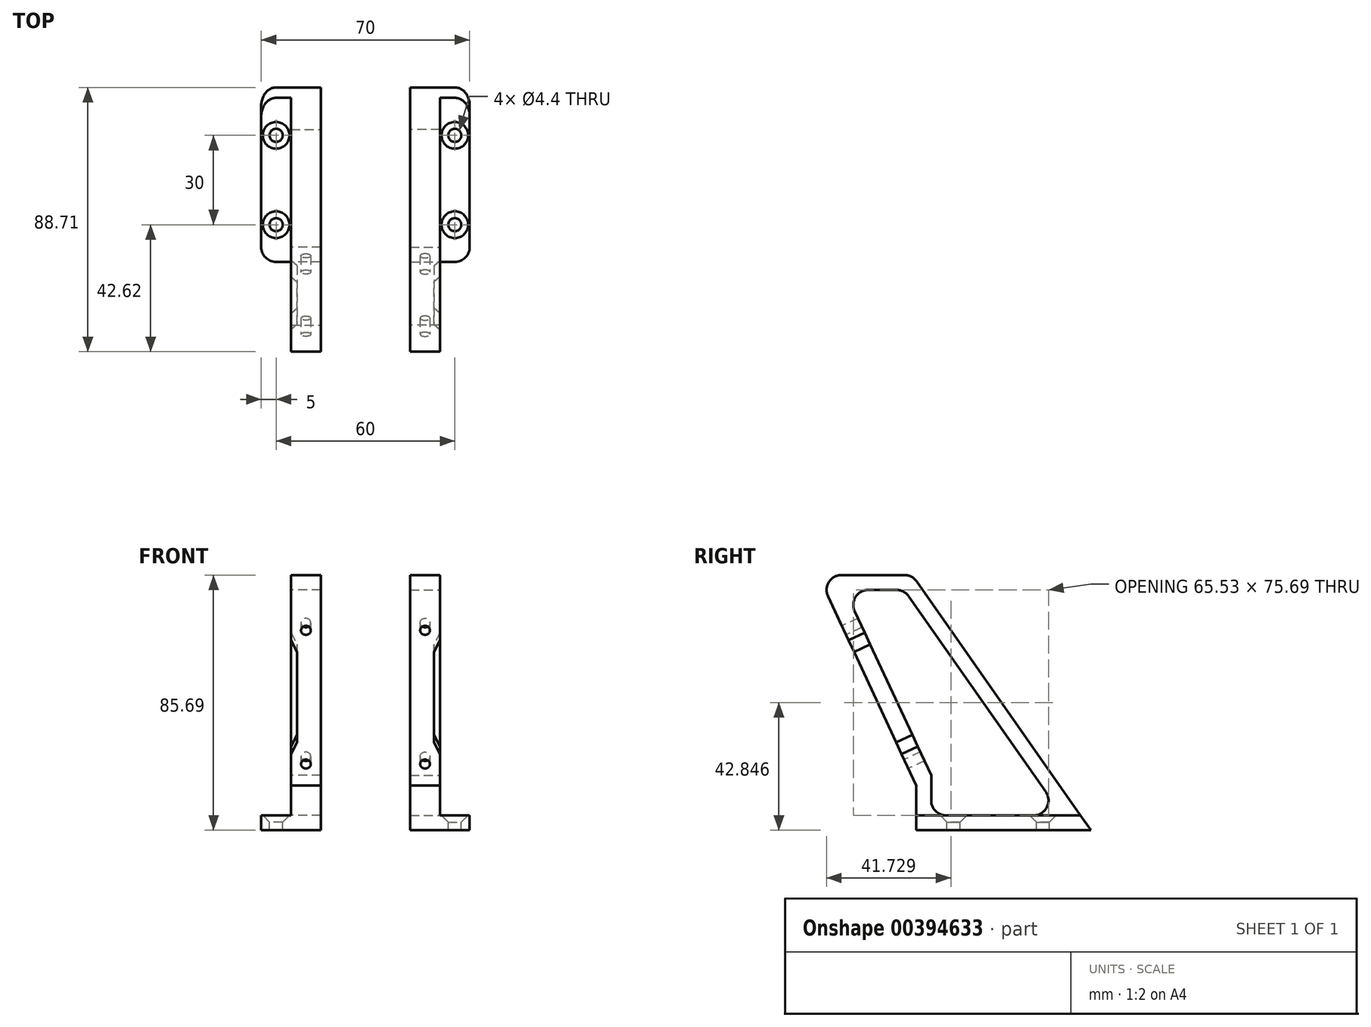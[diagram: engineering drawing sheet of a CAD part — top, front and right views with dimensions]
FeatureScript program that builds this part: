
annotation { "Feature Type Name" : "Feature", "Feature Type Description" : "" }
export const myFeature = defineFeature(function(context is Context, id is Id, definition is map)
    precondition{}
    {
        {
            var Q0;
            Q0=qCreatedBy(makeId("Right.planeOp"),FACE);
            var sketch = newSketch(context, id + "F0", { "sketchPlane" : qUnion([Q0])});
            skLineSegment(sketch, "E0", {"start": v(0, 0) * mm, "end": v(0, 15) * mm});
            skLineSegment(sketch, "E1", {"start": v(0, 15) * mm, "end": v(-32.96, 85.7) * mm});
            skLineSegment(sketch, "E2", {"start": v(-32.96, 85.7) * mm, "end": v(-1.4, 85.7) * mm});
            skLineSegment(sketch, "E3", {"start": v(-1.4, 85.7) * mm, "end": v(58.6, 0) * mm});
            skLineSegment(sketch, "E4", {"start": v(58.6, 0) * mm, "end": v(0, 0) * mm});
            skLineSegment(sketch, "E5", {"start": v(48.99, 5) * mm, "end": v(5, 5) * mm});
            skLineSegment(sketch, "E6", {"start": v(5, 5) * mm, "end": v(5, 18.47) * mm});
            skLineSegment(sketch, "E7", {"start": v(5, 18.47) * mm, "end": v(-24.01, 80.7) * mm});
            skLineSegment(sketch, "E8", {"start": v(-24.01, 80.7) * mm, "end": v(-4.01, 80.7) * mm});
            skLineSegment(sketch, "E9", {"start": v(-4.01, 80.7) * mm, "end": v(48.99, 5) * mm});
            skSolve(sketch);
        }
        {
            var Q0;
            Q0=makeQuery(id+"F0.imprint","IMPRINT",FACE,{"disambiguationData":[TD([[makeQuery(id+"F0.imprint","IMPRINT",EDGE,{"derivedFrom":sQuery(id+"F0.wireOp",EDGE,"E0")}),-1.0]])]});
            extrude(context, id + "F1", {"entities" : qUnion([Q0]), "depth" : 10 * mm, "offsetDistance" : 25 * mm});
        }
        {
            var Q0;
            Q0=makeQuery(id+"F1.opExtrude","CAP_FACE",FACE,{"disambiguationData":[OSD([sQuery(id+"F0.wireOp",EDGE,"E0"),sQuery(id+"F0.wireOp",EDGE,"E1"),sQuery(id+"F0.wireOp",EDGE,"E2"),sQuery(id+"F0.wireOp",EDGE,"E3"),sQuery(id+"F0.wireOp",EDGE,"E4"),sQuery(id+"F0.wireOp",EDGE,"E5"),sQuery(id+"F0.wireOp",EDGE,"E6"),sQuery(id+"F0.wireOp",EDGE,"E7"),sQuery(id+"F0.wireOp",EDGE,"E8"),sQuery(id+"F0.wireOp",EDGE,"E9")])],"isStart":true});
            var sketch = newSketch(context, id + "F2", { "sketchPlane" : qUnion([Q0])});
            skLineSegment(sketch, "E10", {"start": v(-55.1, 5) * mm, "end": v(0, 5) * mm});
            skSolve(sketch);
        }
        {
            var Q0;
            {var subQ4=makeQuery(id+"F1.opExtrude","CAP_EDGE",EDGE,{"disambiguationData":[OSD([sQuery(id+"F0.wireOp",EDGE,"E4")])],"isStart":true});Q0=makeQuery(id+"F2.imprint","IMPRINT",FACE,{"disambiguationData":[TD([[makeQuery(id+"F2.imprint","IMPRINT",EDGE,{"derivedFrom":subQ4}),1.0]])]});}
            extrude(context, id + "F3", {"entities" : qUnion([Q0]), "operationType" : NewBodyOperationType.ADD, "depth" : 10 * mm, "offsetDistance" : 25 * mm});
        }
        {
            var Q0;
            Q0=makeQuery(id+"F3.opExtrude","CAP_EDGE",EDGE,{"disambiguationData":[OSD([sQuery(id+"F0.wireOp",EDGE,"E3")])],"isStart":false});
            var Q1;
            Q1=makeQuery(id+"F3.opExtrude","CAP_EDGE",EDGE,{"disambiguationData":[OSD([sQuery(id+"F0.wireOp",EDGE,"E0")])],"isStart":false});
            var Q2;
            Q2=makeQuery(id+"F1.opExtrude","SWEPT_EDGE",EDGE,{"disambiguationData":[OSD([sQuery(id+"F0.wireOp",EDGE,"E2"),sQuery(id+"F0.wireOp",EDGE,"E3")])]});
            fillet(context, id + "F4", {"entities" : qUnion([Q0, Q1, Q2]), "radius" : 5 * mm, "tangentPropagation" : true, "allowEdgeOverflow" : false});
        }
        {
            var Q0;
            Q0=makeQuery(id+"F1.opExtrude","SWEPT_FACE",FACE,{"disambiguationData":[OSD([sQuery(id+"F0.wireOp",EDGE,"E1")])]});
            var sketch = newSketch(context, id + "F5", { "sketchPlane" : qUnion([Q0])});
            skPoint(sketch, "E11", {"position": v(5, 71.1) * mm});
            skPoint(sketch, "E11.positionSnap0", {"position": v(5, 91.6) * mm});
            skPoint(sketch, "E12", {"position": v(5, 21.6) * mm});
            skPoint(sketch, "E12.positionSnap0", {"position": v(5, 13.6) * mm});
            skSolve(sketch);
        }
        {
            var Q0;
            Q0=sQuery(id+"F5.wireOp",VERTEX,"E11");
            var Q1;
            Q1=sQuery(id+"F5.wireOp",VERTEX,"E12");
            var Q2;
            Q2=makeQuery(id+"F1.opExtrude","SWEPT_BODY",BODY,{"disambiguationData":[OSD([sQuery(id+"F0.wireOp",EDGE,"E0"),sQuery(id+"F0.wireOp",EDGE,"E1"),sQuery(id+"F0.wireOp",EDGE,"E2"),sQuery(id+"F0.wireOp",EDGE,"E3"),sQuery(id+"F0.wireOp",EDGE,"E4"),sQuery(id+"F0.wireOp",EDGE,"E5"),sQuery(id+"F0.wireOp",EDGE,"E6"),sQuery(id+"F0.wireOp",EDGE,"E7"),sQuery(id+"F0.wireOp",EDGE,"E8"),sQuery(id+"F0.wireOp",EDGE,"E9")])]});
            hole(context, id + "F6", {"style" : HoleStyle.SIMPLE, "endStyle" : HoleEndStyle.BLIND, "standardTappedOrClearance" : lookupTablePath({ "standard" : "ISO", "fit" : "Normal", "size" : "M3", "type" : "Clearance" }), "standardBlindInLast" : lookupTablePath({ "fit" : "Standard", "standard" : "ISO", "size" : "M3", "type" : "Clearance" }), "holeDiameter" : 3.3 * mm, "majorDiameter" : 5 * mm, "holeDepth" : 10 * mm, "isTappedThrough" : true, "tappedDepth" : 12 * mm, "tapClearance" : 3, "locations" : qUnion([Q0, Q1]), "scope" : qUnion([Q2])});
        }
        {
            var Q0;
            Q0=makeQuery(id+"F1.opExtrude","SWEPT_FACE",FACE,{"disambiguationData":[OSD([sQuery(id+"F0.wireOp",EDGE,"E7")])]});
            var sketch = newSketch(context, id + "F7", { "sketchPlane" : qUnion([Q0])});
            skCircle(sketch, "E13.cCircle", {"center": v(-5, 21.6) * mm, "radius": 2.75 * mm, "construction": true});
            skLineSegment(sketch, "E13.0", {"start": v(-7.75, 20) * mm, "end": v(-7.75, 23.18) * mm});
            skLineSegment(sketch, "E13.1", {"start": v(-7.75, 23.18) * mm, "end": v(-5, 24.77) * mm});
            skLineSegment(sketch, "E13.2", {"start": v(-5, 24.77) * mm, "end": v(-2.25, 23.18) * mm});
            skLineSegment(sketch, "E13.3", {"start": v(-2.25, 23.18) * mm, "end": v(-2.25, 20) * mm});
            skLineSegment(sketch, "E13.4", {"start": v(-2.25, 20) * mm, "end": v(-5, 18.42) * mm});
            skLineSegment(sketch, "E13.5", {"start": v(-5, 18.42) * mm, "end": v(-7.75, 20) * mm});
            skPoint(sketch, "E13.0.midPoint", {"position": v(-7.75, 21.6) * mm});
            skCircle(sketch, "E14.cCircle", {"center": v(-5, 71.1) * mm, "radius": 2.75 * mm, "construction": true});
            skLineSegment(sketch, "E14.0", {"start": v(-7.75, 69.5) * mm, "end": v(-7.75, 72.68) * mm});
            skLineSegment(sketch, "E14.1", {"start": v(-7.75, 72.68) * mm, "end": v(-5, 74.27) * mm});
            skLineSegment(sketch, "E14.2", {"start": v(-5, 74.27) * mm, "end": v(-2.25, 72.68) * mm});
            skLineSegment(sketch, "E14.3", {"start": v(-2.25, 72.68) * mm, "end": v(-2.25, 69.5) * mm});
            skLineSegment(sketch, "E14.4", {"start": v(-2.25, 69.5) * mm, "end": v(-5, 67.92) * mm});
            skLineSegment(sketch, "E14.5", {"start": v(-5, 67.92) * mm, "end": v(-7.75, 69.5) * mm});
            skPoint(sketch, "E14.0.midPoint", {"position": v(-7.75, 71.1) * mm});
            skSolve(sketch);
        }
        {
            var Q0;
            Q0=makeQuery(id+"F1.opExtrude","SWEPT_EDGE",EDGE,{"disambiguationData":[OSD([sQuery(id+"F0.wireOp",EDGE,"E1"),sQuery(id+"F0.wireOp",EDGE,"E2")])]});
            var Q1;
            Q1=makeQuery(id+"F1.opExtrude","SWEPT_EDGE",EDGE,{"disambiguationData":[OSD([sQuery(id+"F0.wireOp",EDGE,"E7"),sQuery(id+"F0.wireOp",EDGE,"E8")])]});
            var Q2;
            Q2=makeQuery(id+"F1.opExtrude","SWEPT_EDGE",EDGE,{"disambiguationData":[OSD([sQuery(id+"F0.wireOp",EDGE,"E8"),sQuery(id+"F0.wireOp",EDGE,"E9")])]});
            var Q3;
            Q3=makeQuery(id+"F1.opExtrude","SWEPT_EDGE",EDGE,{"disambiguationData":[OSD([sQuery(id+"F0.wireOp",EDGE,"E5"),sQuery(id+"F0.wireOp",EDGE,"E6")])]});
            var Q4;
            Q4=makeQuery(id+"F1.opExtrude","SWEPT_EDGE",EDGE,{"disambiguationData":[OSD([sQuery(id+"F0.wireOp",EDGE,"E5"),sQuery(id+"F0.wireOp",EDGE,"E9")])]});
            fillet(context, id + "F8", {"entities" : qUnion([Q0, Q1, Q2, Q3, Q4]), "radius" : 5 * mm, "tangentPropagation" : true, "allowEdgeOverflow" : false});
        }
        {
            var Q0;
            Q0=makeQuery(id+"F1.opExtrude","SWEPT_FACE",FACE,{"disambiguationData":[OSD([sQuery(id+"F0.wireOp",EDGE,"E1")])]});
            var sketch = newSketch(context, id + "F9", { "sketchPlane" : qUnion([Q0])});
            skLineSegment(sketch, "E15", {"start": v(2, 63.1) * mm, "end": v(2, 29.6) * mm});
            skLineSegment(sketch, "E16", {"start": v(2, 63.1) * mm, "end": v(0, 67.38) * mm});
            skLineSegment(sketch, "E17", {"start": v(0, 25.3) * mm, "end": v(2, 29.6) * mm});
            skSolve(sketch);
        }
        {
            var Q0;
            Q0=makeQuery(id+"F9.imprint","IMPRINT",FACE,{"disambiguationData":[TD([[makeQuery(id+"F9.imprint","IMPRINT",EDGE,{"derivedFrom":sQuery(id+"F9.wireOp",EDGE,"E15")}),-1.0]])]});
            extrude(context, id + "F10", {"entities" : qUnion([Q0]), "operationType" : NewBodyOperationType.REMOVE, "endBound" : BoundingType.UP_TO_NEXT, "oppositeDirection" : true, "depth" : 25 * mm, "offsetDistance" : 25 * mm});
        }
        {
            var Q0;
            Q0=makeQuery(id+"F1.opExtrude","CAP_FACE",FACE,{"disambiguationData":[OSD([sQuery(id+"F0.wireOp",EDGE,"E0"),sQuery(id+"F0.wireOp",EDGE,"E1"),sQuery(id+"F0.wireOp",EDGE,"E2"),sQuery(id+"F0.wireOp",EDGE,"E3"),sQuery(id+"F0.wireOp",EDGE,"E4"),sQuery(id+"F0.wireOp",EDGE,"E5"),sQuery(id+"F0.wireOp",EDGE,"E6"),sQuery(id+"F0.wireOp",EDGE,"E7"),sQuery(id+"F0.wireOp",EDGE,"E8"),sQuery(id+"F0.wireOp",EDGE,"E9")])],"isStart":false});
            cPlane(context, id + "F11", {"entities" : qUnion([Q0]), "cplaneType" : CPlaneType.OFFSET, "offset" : 15 * mm, "width" : 150 * mm, "height" : 150 * mm});
        }
        {
            var Q0;
            Q0=makeQuery(id+"F3.boolean.opBoolean","MERGE",FACE,{"derivedFrom":[makeQuery(id+"F1.opExtrude","SWEPT_FACE",FACE,{"disambiguationData":[OSD([sQuery(id+"F0.wireOp",EDGE,"E5")])]}),makeQuery(id+"F3.opExtrude","SWEPT_FACE",FACE,{"disambiguationData":[OSD([sQuery(id+"F2.wireOp",EDGE,"E10")])]})]});
            var sketch = newSketch(context, id + "F12", { "sketchPlane" : qUnion([Q0])});
            skPoint(sketch, "E18", {"position": v(-5, 42.5) * mm});
            skPoint(sketch, "E19", {"position": v(-5, 12.5) * mm});
            skLineSegment(sketch, "E20", {"start": v(-5, 0) * mm, "end": v(-5, 55.1) * mm, "construction": true});
            skSolve(sketch);
        }
        {
            var Q0;
            Q0=sQuery(id+"F12.wireOp",VERTEX,"E18");
            var Q1;
            Q1=sQuery(id+"F12.wireOp",VERTEX,"E19");
            var Q2;
            Q2=makeQuery(id+"F1.opExtrude","SWEPT_BODY",BODY,{"disambiguationData":[OSD([sQuery(id+"F0.wireOp",EDGE,"E0"),sQuery(id+"F0.wireOp",EDGE,"E1"),sQuery(id+"F0.wireOp",EDGE,"E2"),sQuery(id+"F0.wireOp",EDGE,"E3"),sQuery(id+"F0.wireOp",EDGE,"E4"),sQuery(id+"F0.wireOp",EDGE,"E5"),sQuery(id+"F0.wireOp",EDGE,"E6"),sQuery(id+"F0.wireOp",EDGE,"E7"),sQuery(id+"F0.wireOp",EDGE,"E8"),sQuery(id+"F0.wireOp",EDGE,"E9")])]});
            hole(context, id + "F13", {"style" : HoleStyle.C_SINK, "endStyle" : HoleEndStyle.BLIND, "standardTappedOrClearance" : lookupTablePath({ "standard" : "ISO", "fit" : "Normal", "size" : "M4", "type" : "Clearance" }), "standardBlindInLast" : lookupTablePath({ "fit" : "Standard", "standard" : "ISO", "size" : "M4", "type" : "Clearance" }), "holeDiameter" : 4.4 * mm, "cSinkDiameter" : 8.96 * mm, "cSinkAngle" : 90 * degree, "majorDiameter" : 5 * mm, "holeDepth" : 10 * mm, "isTappedThrough" : true, "tappedDepth" : 12 * mm, "tapClearance" : 3, "locations" : qUnion([Q0, Q1]), "scope" : qUnion([Q2])});
        }
        {
            var Q0;
            Q0=makeQuery(id+"F1.opExtrude","SWEPT_BODY",BODY,{"disambiguationData":[OSD([sQuery(id+"F0.wireOp",EDGE,"E0"),sQuery(id+"F0.wireOp",EDGE,"E1"),sQuery(id+"F0.wireOp",EDGE,"E2"),sQuery(id+"F0.wireOp",EDGE,"E3"),sQuery(id+"F0.wireOp",EDGE,"E4"),sQuery(id+"F0.wireOp",EDGE,"E5"),sQuery(id+"F0.wireOp",EDGE,"E6"),sQuery(id+"F0.wireOp",EDGE,"E7"),sQuery(id+"F0.wireOp",EDGE,"E8"),sQuery(id+"F0.wireOp",EDGE,"E9")])]});
            var Q1;
            Q1=qCreatedBy(id+"F11.planeOp",FACE);
            mirror(context, id + "F14", {"entities" : qUnion([Q0]), "mirrorPlane" : qUnion([Q1])});
        }
    });
